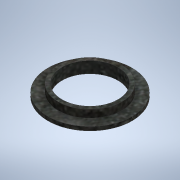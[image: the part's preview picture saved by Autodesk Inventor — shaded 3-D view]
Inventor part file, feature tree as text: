
AUTODESK INVENTOR PART (.ipt)
format: ipt  version: 2020.2 (Build 242310000, 310)  size: 115,712 bytes
history: native  units: mm
features: extrude x2, other x1, sketch x1
ambient origin geometry x8: Origin, YZ Plane, XZ Plane, XY Plane, X Axis, Y Axis, Z Axis, Center Point
bodies: Body1 (feature_tree)
feature tree (4):
  other  "ソリッド1"
  sketch  "スケッチ1"
  extrude  "押し出し1"  Depth=22.0mm
  extrude  "押し出し2"  Depth=25.0mm
